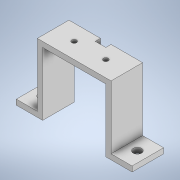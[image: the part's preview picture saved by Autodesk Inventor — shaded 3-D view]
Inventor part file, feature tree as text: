
AUTODESK INVENTOR PART (.ipt)
format: ipt  version: 2020 (Build 240168000, 168)  size: 287,232 bytes
history: native  units: mm
features: extrude x2, hole x2, sketch x2, projected_geometry x2, other x1
ambient origin geometry x8: Origin, YZ Plane, XZ Plane, XY Plane, X Axis, Y Axis, Z Axis, Center Point
bodies: Body1 (feature_tree)
feature tree (9):
  other  "솔리드1"
  extrude  "돌출1"  Depth=60.0mm
  hole  "구멍1"  [1 undecoded]
  hole  "구멍2"  [1 undecoded]
  extrude  "돌출2"  Depth=5.0mm
  sketch  "스케치1"
  sketch  "스케치3"
  projected_geometry  "투영된 루프1"
  projected_geometry  "투영된 루프2"
note: 2 required parameter values undecoded (feature->parameter linkage not recoverable at this tier; creation-order binding heuristic only, values carry confidence <= 0.55)
